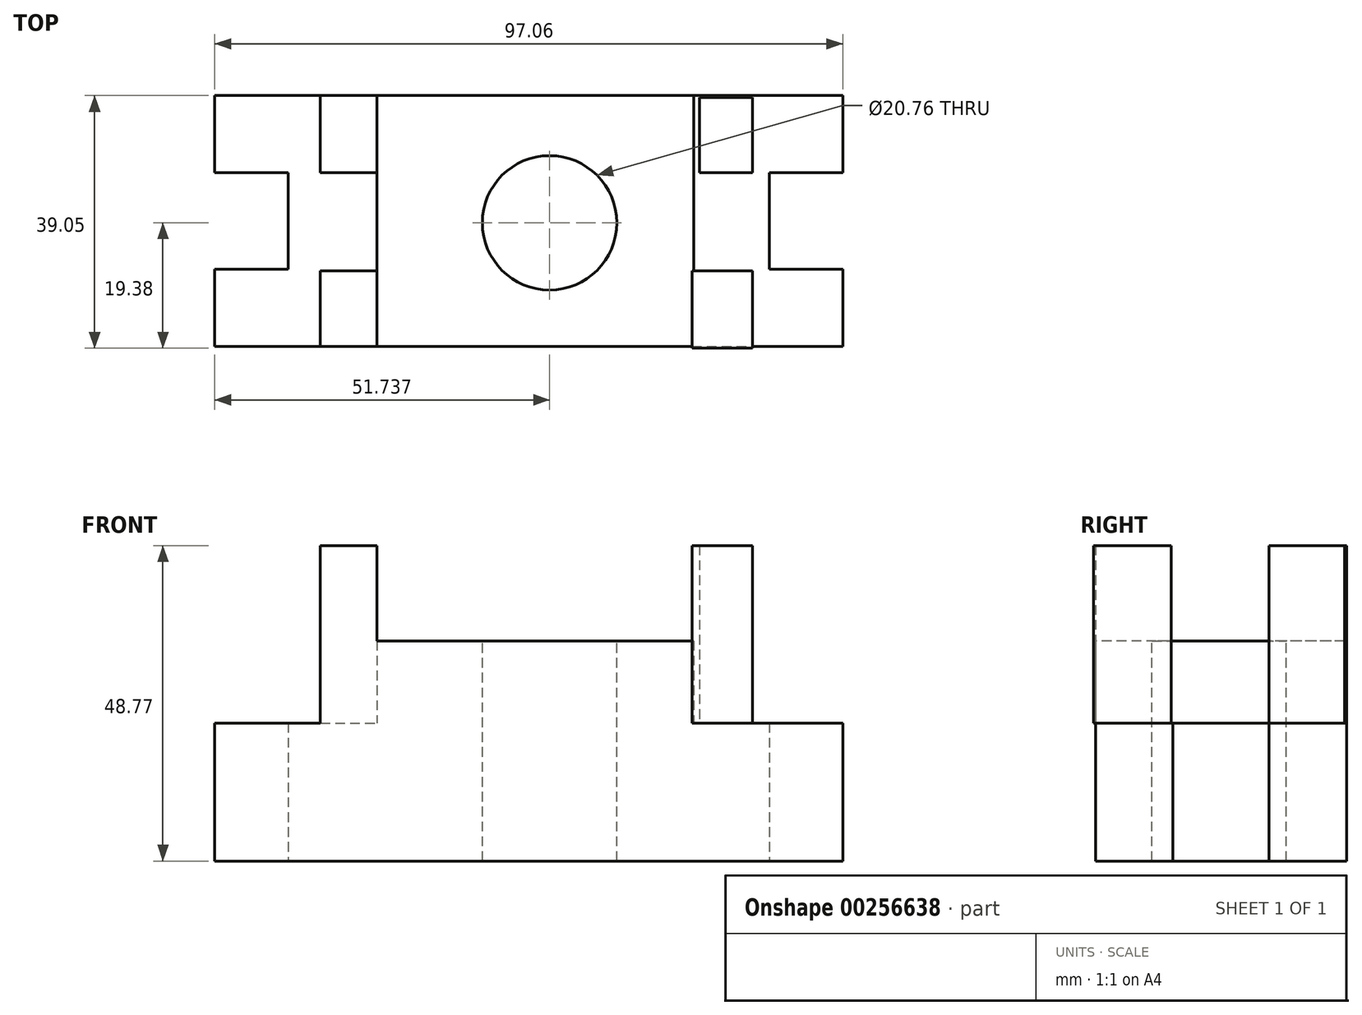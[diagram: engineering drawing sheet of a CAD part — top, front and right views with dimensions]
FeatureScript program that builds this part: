
annotation { "Feature Type Name" : "Feature", "Feature Type Description" : "" }
export const myFeature = defineFeature(function(context is Context, id is Id, definition is map)
    precondition{}
    {
        {
            var Q0;
            Q0=qCreatedBy(makeId("Top.planeOp"),FACE);
            var sketch = newSketch(context, id + "F0", { "sketchPlane" : qUnion([Q0])});
            skLineSegment(sketch, "E0.bottom", {"start": v(-34.1, -19.1) * mm, "end": v(40.22, -19.1) * mm});
            skLineSegment(sketch, "E0.top", {"start": v(-34.1, 19.67) * mm, "end": v(40.22, 19.67) * mm});
            skLineSegment(sketch, "E0.left", {"start": v(-34.1, -19.1) * mm, "end": v(-34.1, 19.67) * mm});
            skLineSegment(sketch, "E0.right", {"start": v(40.22, -19.1) * mm, "end": v(40.22, 19.67) * mm});
            skLineSegment(sketch, "E1.bottom", {"start": v(40.22, 19.67) * mm, "end": v(51.6, 19.67) * mm});
            skLineSegment(sketch, "E1.top", {"start": v(40.22, 7.72) * mm, "end": v(51.6, 7.72) * mm});
            skLineSegment(sketch, "E1.left", {"start": v(40.22, 19.67) * mm, "end": v(40.22, 7.72) * mm});
            skLineSegment(sketch, "E1.right", {"start": v(51.6, 19.67) * mm, "end": v(51.6, 7.72) * mm});
            skLineSegment(sketch, "E2.bottom", {"start": v(40.22, -19.1) * mm, "end": v(51.6, -19.1) * mm});
            skLineSegment(sketch, "E2.top", {"start": v(40.22, -7.14) * mm, "end": v(51.6, -7.14) * mm});
            skLineSegment(sketch, "E2.left", {"start": v(40.22, -19.1) * mm, "end": v(40.22, -7.14) * mm});
            skLineSegment(sketch, "E2.right", {"start": v(51.6, -19.1) * mm, "end": v(51.6, -7.14) * mm});
            skLineSegment(sketch, "E3.bottom", {"start": v(-34.1, 7.72) * mm, "end": v(-45.47, 7.72) * mm});
            skLineSegment(sketch, "E3.top", {"start": v(-34.1, 19.67) * mm, "end": v(-45.47, 19.67) * mm});
            skLineSegment(sketch, "E3.left", {"start": v(-34.1, 7.72) * mm, "end": v(-34.1, 19.67) * mm});
            skLineSegment(sketch, "E3.right", {"start": v(-45.47, 7.72) * mm, "end": v(-45.47, 19.67) * mm});
            skLineSegment(sketch, "E4.bottom", {"start": v(-45.47, -7.14) * mm, "end": v(-34.1, -7.14) * mm});
            skLineSegment(sketch, "E4.top", {"start": v(-45.47, -19.1) * mm, "end": v(-34.1, -19.1) * mm});
            skLineSegment(sketch, "E4.left", {"start": v(-45.47, -7.14) * mm, "end": v(-45.47, -19.1) * mm});
            skLineSegment(sketch, "E4.right", {"start": v(-34.1, -7.14) * mm, "end": v(-34.1, -19.1) * mm});
            skSolve(sketch);
        }
        {
            var Q0;
            Q0 = qSketchRegion(id + "F0", true);
            extrude(context, id + "F1", {"entities" : qUnion([Q0]), "depth" : 21.34 * mm});
        }
        {
            var Q0;
            Q0=makeQuery(id+"F1.opExtrude","CAP_FACE",FACE,{"disambiguationData":[OSD([sQuery(id+"F0.wireOp",EDGE,"E0.bottom"),sQuery(id+"F0.wireOp",EDGE,"E0.top"),sQuery(id+"F0.wireOp",EDGE,"E0.left"),sQuery(id+"F0.wireOp",EDGE,"E0.right"),sQuery(id+"F0.wireOp",EDGE,"E1.bottom"),sQuery(id+"F0.wireOp",EDGE,"E1.top"),sQuery(id+"F0.wireOp",EDGE,"E1.right"),sQuery(id+"F0.wireOp",EDGE,"E2.bottom"),sQuery(id+"F0.wireOp",EDGE,"E2.top"),sQuery(id+"F0.wireOp",EDGE,"E2.right"),sQuery(id+"F0.wireOp",EDGE,"E3.bottom"),sQuery(id+"F0.wireOp",EDGE,"E3.top"),sQuery(id+"F0.wireOp",EDGE,"E3.right"),sQuery(id+"F0.wireOp",EDGE,"E4.bottom"),sQuery(id+"F0.wireOp",EDGE,"E4.top"),sQuery(id+"F0.wireOp",EDGE,"E4.left")])],"isStart":false});
            var sketch = newSketch(context, id + "F2", { "sketchPlane" : qUnion([Q0])});
            skLineSegment(sketch, "E5.bottom", {"start": v(-20.4, 19.67) * mm, "end": v(28.56, 19.67) * mm});
            skLineSegment(sketch, "E5.top", {"start": v(-20.4, -19.1) * mm, "end": v(28.56, -19.1) * mm});
            skLineSegment(sketch, "E5.left", {"start": v(-20.4, 19.67) * mm, "end": v(-20.4, -19.1) * mm});
            skLineSegment(sketch, "E5.right", {"start": v(28.56, 19.67) * mm, "end": v(28.56, -19.1) * mm});
            skSolve(sketch);
        }
        {
            var Q0;
            Q0 = qSketchRegion(id + "F2", true);
            extrude(context, id + "F3", {"entities" : qUnion([Q0]), "operationType" : NewBodyOperationType.ADD, "depth" : 12.7 * mm});
        }
        {
            var Q0;
            {var subQ0=sQuery(id+"F0.wireOp",EDGE,"E3.bottom");var subQ1=sQuery(id+"F0.wireOp",EDGE,"E3.top");var subQ2=sQuery(id+"F0.wireOp",EDGE,"E1.bottom");var subQ3=sQuery(id+"F0.wireOp",EDGE,"E0.top");var subQ4=sQuery(id+"F0.wireOp",EDGE,"E0.left");var subQ5=sQuery(id+"F0.wireOp",EDGE,"E4.top");var subQ6=sQuery(id+"F0.wireOp",EDGE,"E2.bottom");var subQ7=sQuery(id+"F0.wireOp",EDGE,"E0.bottom");var subQ8=sQuery(id+"F0.wireOp",EDGE,"E4.left");var subQ9=sQuery(id+"F0.wireOp",EDGE,"E3.right");var subQ10=sQuery(id+"F0.wireOp",EDGE,"E4.bottom");Q0=makeQuery(id+"F3.boolean.opBoolean","SPLIT",FACE,{"disambiguationData":[TD([makeQuery(id+"F1.opExtrude","SWEPT_FACE",FACE,{"disambiguationData":[OSD([subQ4])]})])],"derivedFrom":makeQuery(id+"F1.opExtrude","CAP_FACE",FACE,{"disambiguationData":[OSD([subQ7,subQ3,subQ4,sQuery(id+"F0.wireOp",EDGE,"E0.right"),subQ2,sQuery(id+"F0.wireOp",EDGE,"E1.top"),sQuery(id+"F0.wireOp",EDGE,"E1.right"),subQ6,sQuery(id+"F0.wireOp",EDGE,"E2.top"),sQuery(id+"F0.wireOp",EDGE,"E2.right"),subQ0,subQ1,subQ9,subQ10,subQ5,subQ8])],"isStart":false})});}
            var sketch = newSketch(context, id + "F4", { "sketchPlane" : qUnion([Q0])});
            skLineSegment(sketch, "E6.bottom", {"start": v(-29.15, 19.67) * mm, "end": v(-20.4, 19.67) * mm});
            skLineSegment(sketch, "E6.top", {"start": v(-29.15, 7.72) * mm, "end": v(-20.4, 7.72) * mm});
            skLineSegment(sketch, "E6.left", {"start": v(-29.15, 19.67) * mm, "end": v(-29.15, 7.72) * mm});
            skLineSegment(sketch, "E6.right", {"start": v(-20.4, 19.67) * mm, "end": v(-20.4, 7.72) * mm});
            skLineSegment(sketch, "E7.bottom", {"start": v(-29.15, -7.43) * mm, "end": v(-20.4, -7.43) * mm});
            skLineSegment(sketch, "E7.top", {"start": v(-29.15, -19.1) * mm, "end": v(-20.4, -19.1) * mm});
            skLineSegment(sketch, "E7.left", {"start": v(-29.15, -7.43) * mm, "end": v(-29.15, -19.1) * mm});
            skLineSegment(sketch, "E7.right", {"start": v(-20.4, -7.43) * mm, "end": v(-20.4, -19.1) * mm});
            skLineSegment(sketch, "E8.bottom", {"start": v(29.44, 7.72) * mm, "end": v(37.6, 7.72) * mm});
            skLineSegment(sketch, "E8.top", {"start": v(29.44, 19.38) * mm, "end": v(37.6, 19.38) * mm});
            skLineSegment(sketch, "E8.left", {"start": v(29.44, 7.72) * mm, "end": v(29.44, 19.38) * mm});
            skLineSegment(sketch, "E8.right", {"start": v(37.6, 7.72) * mm, "end": v(37.6, 19.38) * mm});
            skLineSegment(sketch, "E9.bottom", {"start": v(28.27, -7.43) * mm, "end": v(37.6, -7.43) * mm});
            skLineSegment(sketch, "E9.top", {"start": v(28.27, -19.38) * mm, "end": v(37.6, -19.38) * mm});
            skLineSegment(sketch, "E9.left", {"start": v(28.27, -7.43) * mm, "end": v(28.27, -19.38) * mm});
            skLineSegment(sketch, "E9.right", {"start": v(37.6, -7.43) * mm, "end": v(37.6, -19.38) * mm});
            skSolve(sketch);
        }
        {
            var Q0;
            Q0 = qSketchRegion(id + "F4", true);
            extrude(context, id + "F5", {"entities" : qUnion([Q0]), "operationType" : NewBodyOperationType.ADD, "depth" : 27.43 * mm});
        }
        {
            var Q0;
            Q0=makeQuery(id+"F3.opExtrude","CAP_FACE",FACE,{"disambiguationData":[OSD([sQuery(id+"F2.wireOp",EDGE,"E5.bottom"),sQuery(id+"F2.wireOp",EDGE,"E5.top"),sQuery(id+"F2.wireOp",EDGE,"E5.left"),sQuery(id+"F2.wireOp",EDGE,"E5.right")])],"isStart":false});
            var sketch = newSketch(context, id + "F6", { "sketchPlane" : qUnion([Q0])});
            skCircle(sketch, "E10", {"center": v(6.27, 0) * mm, "radius": 10.38 * mm});
            skSolve(sketch);
        }
        {
            var Q0;
            Q0 = qSketchRegion(id + "F6", true);
            extrude(context, id + "F7", {"entities" : qUnion([Q0]), "operationType" : NewBodyOperationType.REMOVE, "oppositeDirection" : true, "depth" : 76.2 * mm});
        }
    });
